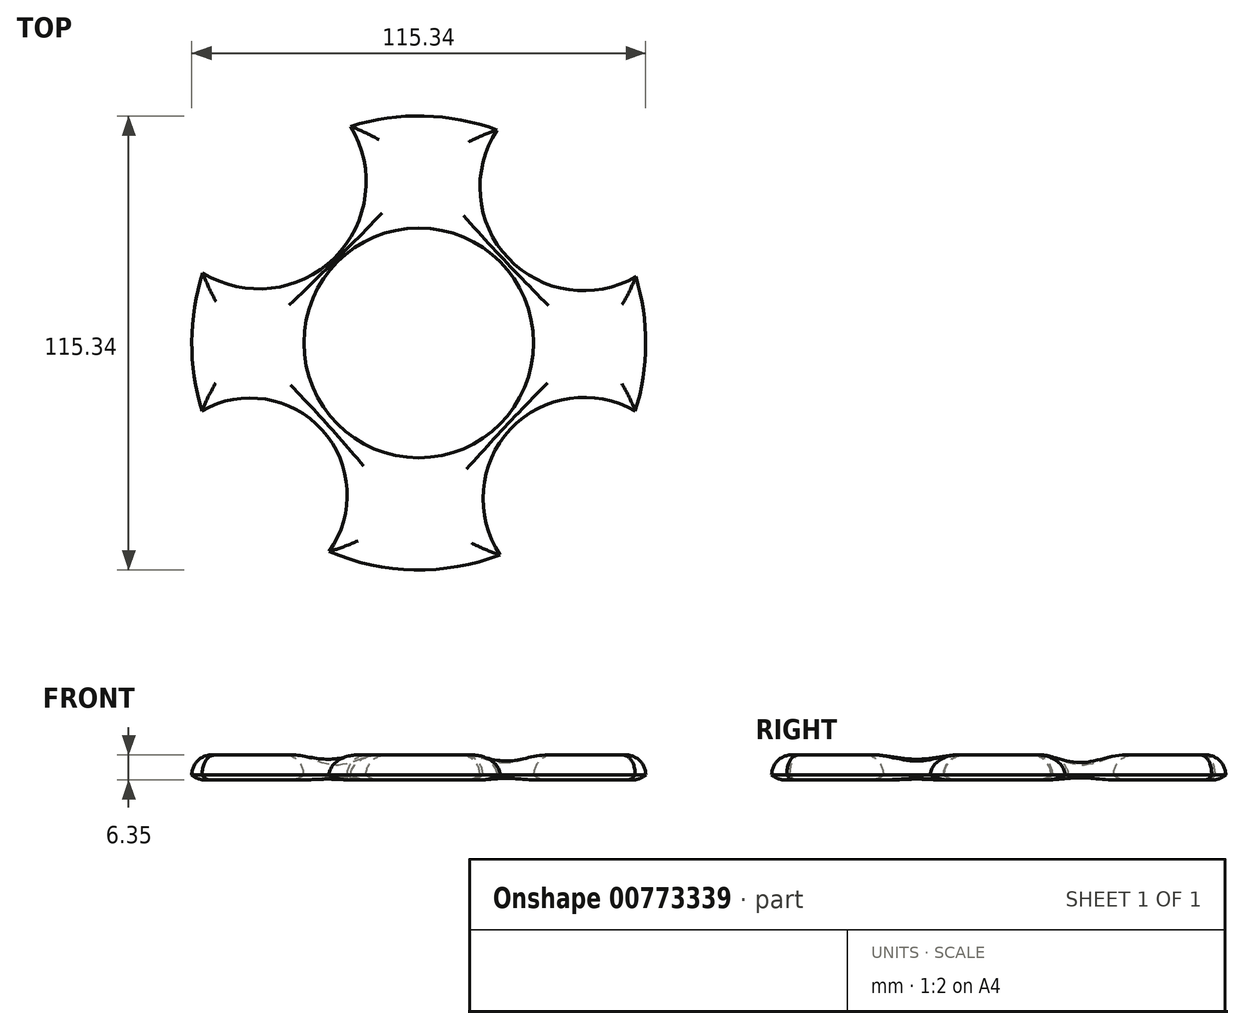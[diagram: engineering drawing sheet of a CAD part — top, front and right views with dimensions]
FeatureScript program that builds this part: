
annotation { "Feature Type Name" : "Feature", "Feature Type Description" : "" }
export const myFeature = defineFeature(function(context is Context, id is Id, definition is map)
    precondition{}
    {
        {
            var Q0;
            Q0=qCreatedBy(makeId("Top.planeOp"),FACE);
            var sketch = newSketch(context, id + "F0", { "sketchPlane" : qUnion([Q0])});
            skCircle(sketch, "E0", {"center": v(0, 0) * mm, "radius": 57.67 * mm});
            skCircle(sketch, "E1", {"center": v(41.9, 39.62) * mm, "radius": 26.35 * mm});
            skCircle(sketch, "E2", {"center": v(-40.6, 40.97) * mm, "radius": 27.23 * mm});
            skCircle(sketch, "E3", {"center": v(42.01, -39.51) * mm, "radius": 25.7 * mm});
            skCircle(sketch, "E4", {"center": v(-42.82, -38.63) * mm, "radius": 24.64 * mm});
            skCircle(sketch, "E5", {"center": v(0, 0) * mm, "radius": 29.19 * mm});
            skSolve(sketch);
        }
        {
            var Q0;
            Q0=makeQuery(id+"F0.imprint","IMPRINT",FACE,{"disambiguationData":[TD([[makeQuery(id+"F0.imprint","IMPRINT",EDGE,{"derivedFrom":sQuery(id+"F0.wireOp",EDGE,"E5")}),-1.0]])]});
            extrude(context, id + "F1", {"entities" : qUnion([Q0]), "depth" : 6.35 * mm, "offsetDistance" : 25.4 * mm});
        }
        {
            var Q0;
            Q0=makeQuery(id+"F1.opExtrude","CAP_FACE",FACE,{"disambiguationData":[OSD([sQuery(id+"F0.wireOp",EDGE,"E1"),sQuery(id+"F0.wireOp",EDGE,"E0"),sQuery(id+"F0.wireOp",EDGE,"E2"),sQuery(id+"F0.wireOp",EDGE,"E3"),sQuery(id+"F0.wireOp",EDGE,"E4"),sQuery(id+"F0.wireOp",EDGE,"E5")])],"isStart":false});
            fillet(context, id + "F2", {"entities" : qUnion([Q0]), "radius" : 5.08 * mm, "tangentPropagation" : true, "allowEdgeOverflow" : false});
        }
        {
            var Q0;
            Q0=makeQuery(id+"F1.opExtrude","CAP_FACE",FACE,{"disambiguationData":[OSD([sQuery(id+"F0.wireOp",EDGE,"E1"),sQuery(id+"F0.wireOp",EDGE,"E0"),sQuery(id+"F0.wireOp",EDGE,"E2"),sQuery(id+"F0.wireOp",EDGE,"E3"),sQuery(id+"F0.wireOp",EDGE,"E4"),sQuery(id+"F0.wireOp",EDGE,"E5")])],"isStart":true});
            fillet(context, id + "F3", {"entities" : qUnion([Q0]), "radius" : 5.08 * mm, "tangentPropagation" : true, "allowEdgeOverflow" : false});
        }
    });
